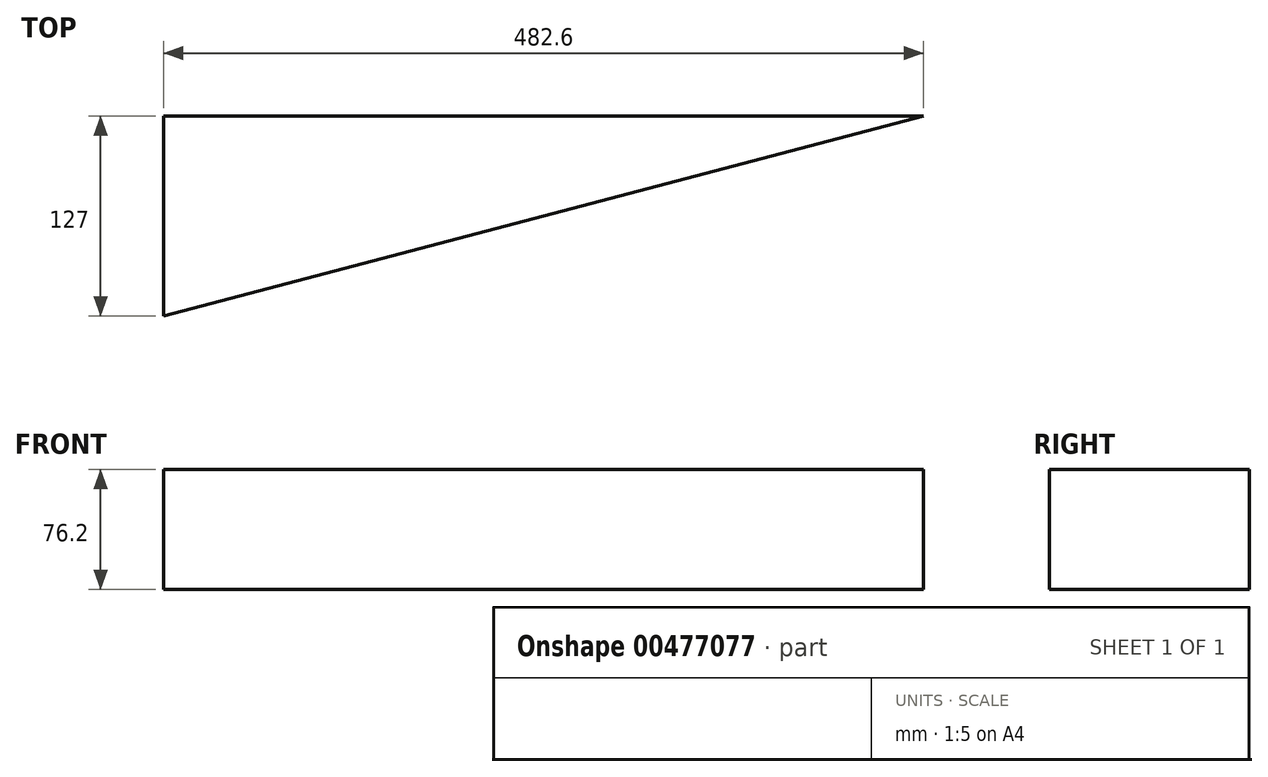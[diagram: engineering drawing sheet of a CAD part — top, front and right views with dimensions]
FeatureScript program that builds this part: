
annotation { "Feature Type Name" : "Feature", "Feature Type Description" : "" }
export const myFeature = defineFeature(function(context is Context, id is Id, definition is map)
    precondition{}
    {
        {
            var Q0;
            Q0=qCreatedBy(makeId("Top.planeOp"),FACE);
            var sketch = newSketch(context, id + "F0", { "sketchPlane" : qUnion([Q0])});
            skLineSegment(sketch, "E0.bottom", {"start": v(241.3, -63.5) * mm, "end": v(-241.3, -63.5) * mm});
            skLineSegment(sketch, "E0.top", {"start": v(241.3, 63.5) * mm, "end": v(-241.3, 63.5) * mm});
            skLineSegment(sketch, "E0.left", {"start": v(241.3, -63.5) * mm, "end": v(241.3, 63.5) * mm});
            skLineSegment(sketch, "E0.right", {"start": v(-241.3, -63.5) * mm, "end": v(-241.3, 63.5) * mm});
            skPoint(sketch, "E0.middle", {"position": v(0, 0) * mm});
            skLineSegment(sketch, "E1", {"start": v(-241.3, -63.5) * mm, "end": v(241.3, 63.5) * mm});
            skSolve(sketch);
        }
        {
            var Q0;
            Q0=makeQuery(id+"F0.imprint","IMPRINT",FACE,{"disambiguationData":[TD([[makeQuery(id+"F0.imprint","IMPRINT",EDGE,{"derivedFrom":sQuery(id+"F0.wireOp",EDGE,"E0.top")}),1.0]])]});
            extrude(context, id + "F1", {"entities" : qUnion([Q0]), "depth" : 76.2 * mm});
        }
    });
